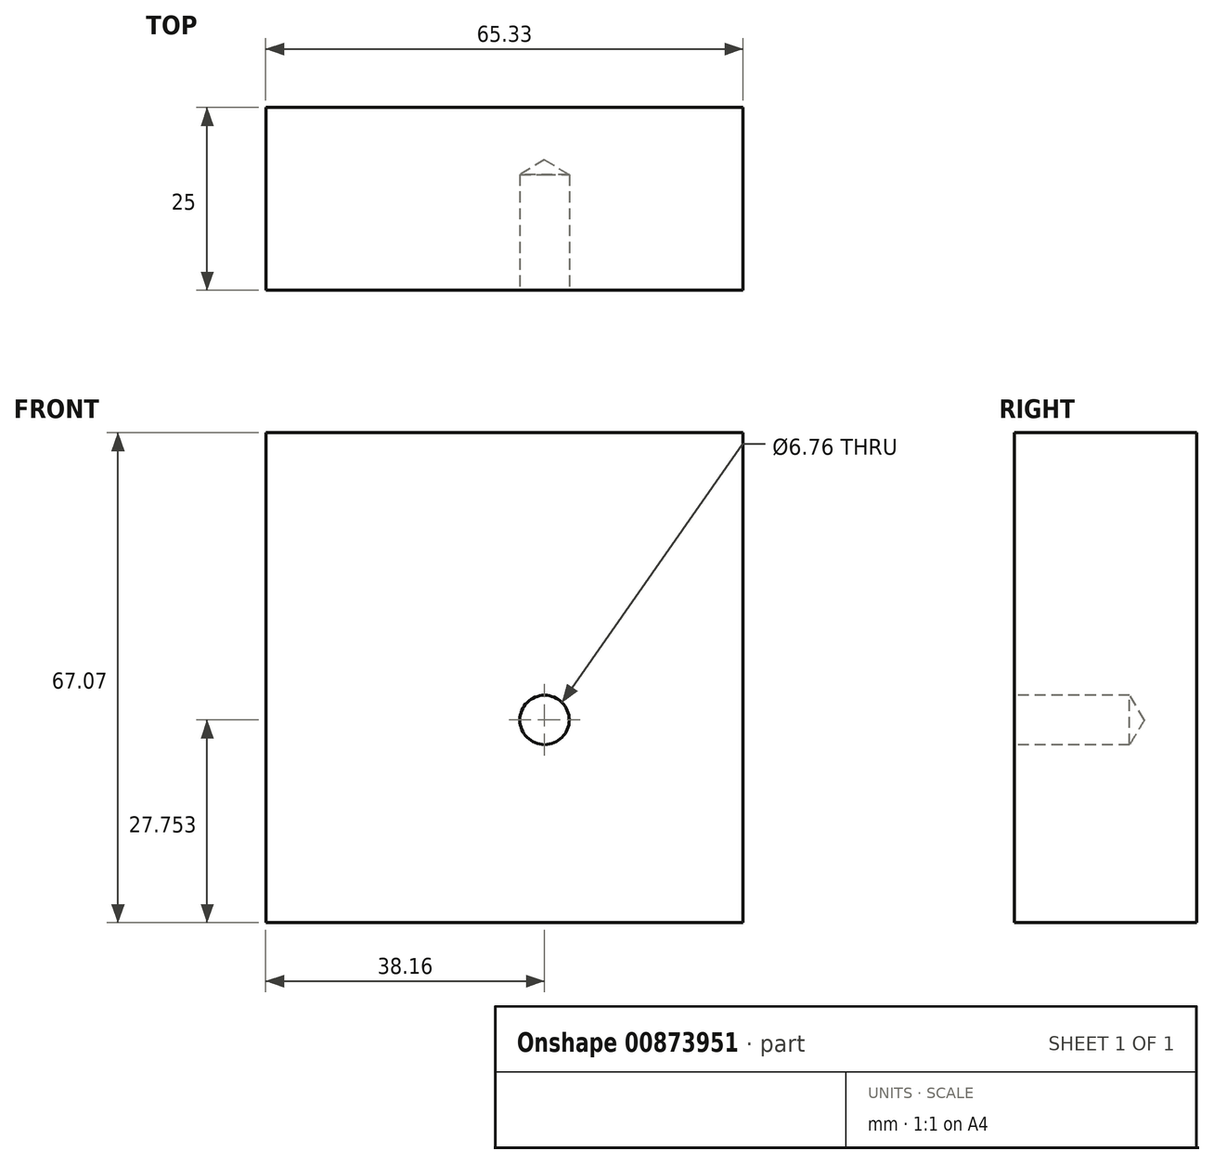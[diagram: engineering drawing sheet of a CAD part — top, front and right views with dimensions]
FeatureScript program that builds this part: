
annotation { "Feature Type Name" : "Feature", "Feature Type Description" : "" }
export const myFeature = defineFeature(function(context is Context, id is Id, definition is map)
    precondition{}
    {
        {
            var Q0;
            Q0=qCreatedBy(makeId("Front.planeOp"),FACE);
            var sketch = newSketch(context, id + "F0", { "sketchPlane" : qUnion([Q0])});
            skLineSegment(sketch, "E0.bottom", {"start": v(-166.94, 28.76) * mm, "end": v(-101.6, 28.76) * mm});
            skLineSegment(sketch, "E0.top", {"start": v(-166.94, 95.83) * mm, "end": v(-101.6, 95.83) * mm});
            skLineSegment(sketch, "E0.left", {"start": v(-166.94, 28.76) * mm, "end": v(-166.94, 95.83) * mm});
            skLineSegment(sketch, "E0.right", {"start": v(-101.6, 28.76) * mm, "end": v(-101.6, 95.83) * mm});
            skPoint(sketch, "E0.middle", {"position": v(-134.27, 62.3) * mm});
            skLineSegment(sketch, "E1.bottom", {"start": v(-49.58, 9.4) * mm, "end": v(-0.43, 9.4) * mm});
            skLineSegment(sketch, "E1.top", {"start": v(-49.58, 73.57) * mm, "end": v(-0.43, 73.57) * mm});
            skLineSegment(sketch, "E1.left", {"start": v(-49.58, 9.4) * mm, "end": v(-49.58, 73.57) * mm});
            skLineSegment(sketch, "E1.right", {"start": v(-0.43, 9.4) * mm, "end": v(-0.43, 73.57) * mm});
            skPoint(sketch, "E1.middle", {"position": v(-25, 41.48) * mm});
            skSolve(sketch);
        }
        {
            var Q0;
            Q0=makeQuery(id+"F0.imprint","IMPRINT",FACE,{"disambiguationData":[TD([[makeQuery(id+"F0.imprint","IMPRINT",EDGE,{"derivedFrom":sQuery(id+"F0.wireOp",EDGE,"E0.bottom")}),1.0]])]});
            extrude(context, id + "F1", {"entities" : qUnion([Q0]), "depth" : 25 * mm, "offsetDistance" : 25 * mm});
        }
        {
            var Q0;
            Q0=makeQuery(id+"F1.opExtrude","CAP_FACE",FACE,{"disambiguationData":[OSD([sQuery(id+"F0.wireOp",EDGE,"E0.bottom"),sQuery(id+"F0.wireOp",EDGE,"E0.top"),sQuery(id+"F0.wireOp",EDGE,"E0.left"),sQuery(id+"F0.wireOp",EDGE,"E0.right")])],"isStart":false});
            var sketch = newSketch(context, id + "F2", { "sketchPlane" : qUnion([Q0])});
            skPoint(sketch, "E2", {"position": v(-128.78, 56.51) * mm});
            skSolve(sketch);
        }
        {
            var Q0;
            Q0=sQuery(id+"F2.wireOp",VERTEX,"E2");
            var Q1;
            Q1=makeQuery(id+"F1.opExtrude","SWEPT_BODY",BODY,{"disambiguationData":[OSD([sQuery(id+"F0.wireOp",EDGE,"E0.bottom"),sQuery(id+"F0.wireOp",EDGE,"E0.top"),sQuery(id+"F0.wireOp",EDGE,"E0.left"),sQuery(id+"F0.wireOp",EDGE,"E0.right")])]});
            hole(context, id + "F3", {"style" : HoleStyle.SIMPLE, "endStyle" : HoleEndStyle.BLIND, "standardTappedOrClearance" : lookupTablePath({ "fit" : "Normal (ASME)", "standard" : "ANSI", "size" : "1/4", "type" : "Clearance" }), "standardBlindInLast" : lookupTablePath({ "fit" : "Free", "standard" : "ANSI", "size" : "1/4", "type" : "Clearance" }), "holeDiameter" : 6.76 * mm, "majorDiameter" : 5 * mm, "holeDepth" : 15.8 * mm, "isTappedThrough" : true, "tappedDepth" : 12 * mm, "tapClearance" : 3, "locations" : qUnion([Q0]), "scope" : qUnion([Q1])});
        }
    });
